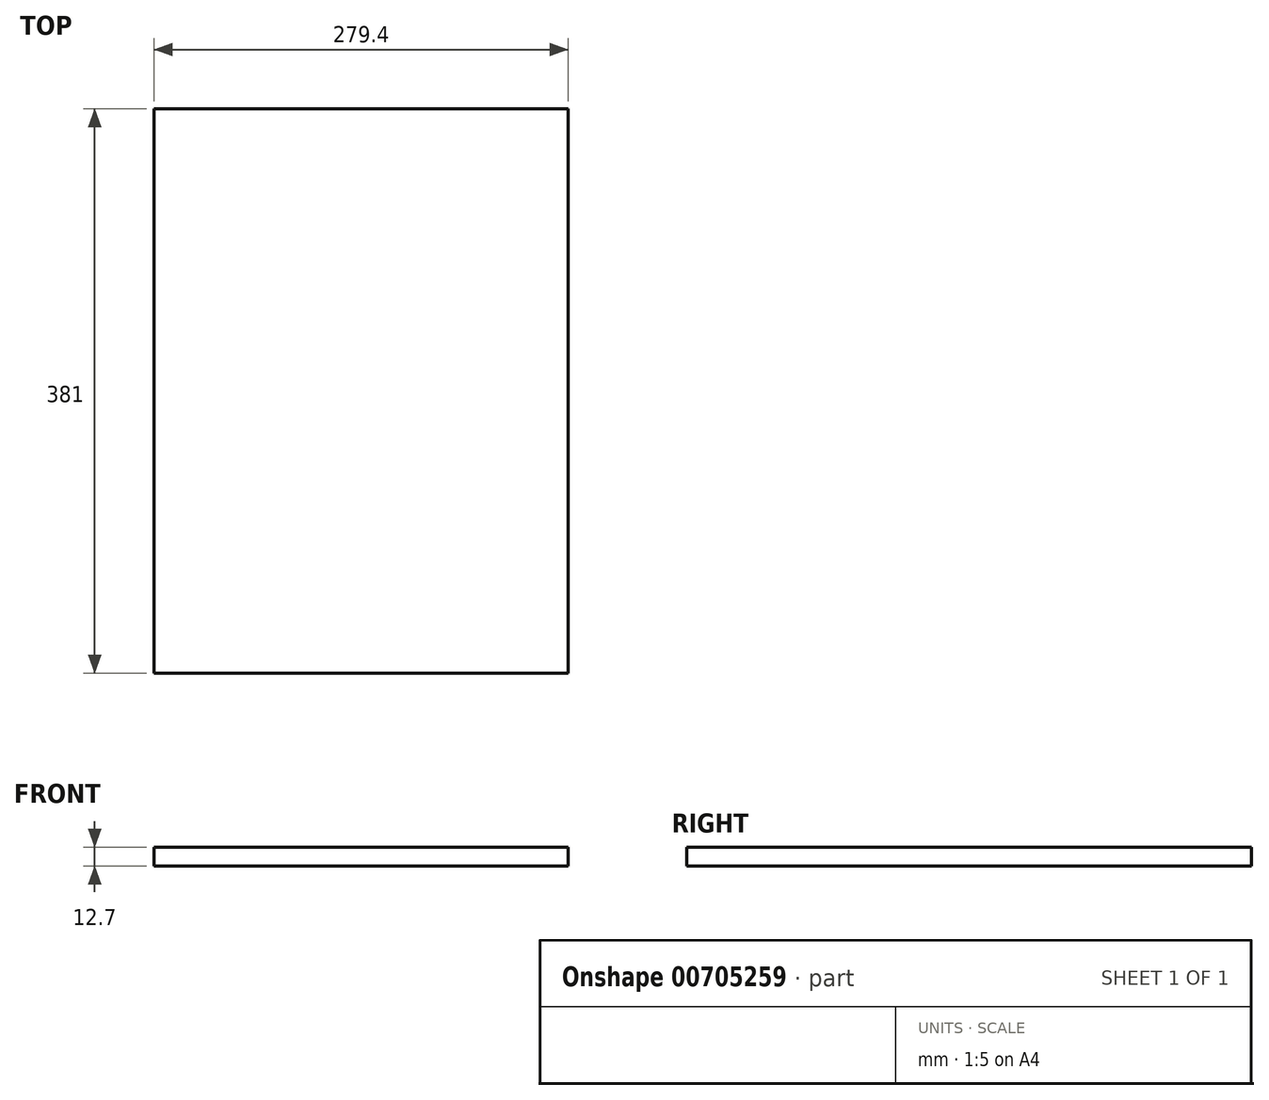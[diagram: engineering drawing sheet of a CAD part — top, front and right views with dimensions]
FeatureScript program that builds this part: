
annotation { "Feature Type Name" : "Feature", "Feature Type Description" : "" }
export const myFeature = defineFeature(function(context is Context, id is Id, definition is map)
    precondition{}
    {
        {
            var Q0;
            Q0=qCreatedBy(makeId("Top.planeOp"),FACE);
            var sketch = newSketch(context, id + "F0", { "sketchPlane" : qUnion([Q0])});
            skLineSegment(sketch, "E0.bottom", {"start": v(-284.48, 203.6) * mm, "end": v(-5.08, 203.6) * mm});
            skLineSegment(sketch, "E0.top", {"start": v(-284.48, -177.4) * mm, "end": v(-5.08, -177.4) * mm});
            skLineSegment(sketch, "E0.left", {"start": v(-284.48, 203.6) * mm, "end": v(-284.48, -177.4) * mm});
            skLineSegment(sketch, "E0.right", {"start": v(-5.08, 203.6) * mm, "end": v(-5.08, -177.4) * mm});
            skSolve(sketch);
        }
        {
            var Q0;
            Q0=makeQuery(id+"F0.imprint","IMPRINT",FACE,{"disambiguationData":[TD([[makeQuery(id+"F0.imprint","IMPRINT",EDGE,{"derivedFrom":sQuery(id+"F0.wireOp",EDGE,"E0.bottom")}),-1.0]])]});
            extrude(context, id + "F1", {"entities" : qUnion([Q0]), "depth" : 12.7 * mm, "offsetDistance" : 25.4 * mm});
        }
    });
